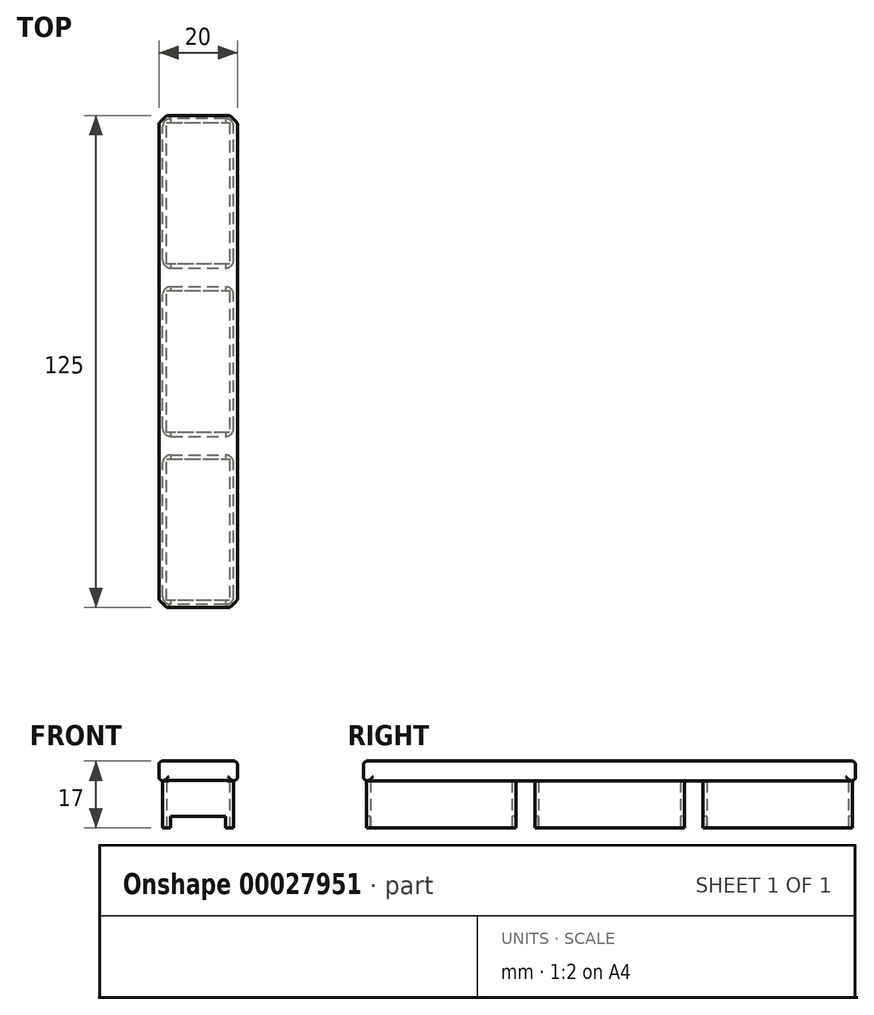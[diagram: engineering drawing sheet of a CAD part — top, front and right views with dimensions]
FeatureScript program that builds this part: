
annotation { "Feature Type Name" : "Feature", "Feature Type Description" : "" }
export const myFeature = defineFeature(function(context is Context, id is Id, definition is map)
    precondition{}
    {
        {
            var Q0;
            Q0=qCreatedBy(makeId("Top.planeOp"),FACE);
            var sketch = newSketch(context, id + "F0", { "sketchPlane" : qUnion([Q0])});
            skLineSegment(sketch, "E0.bottom", {"start": v(-10, 62.5) * mm, "end": v(10, 62.5) * mm});
            skLineSegment(sketch, "E0.top", {"start": v(-10, -62.5) * mm, "end": v(10, -62.5) * mm});
            skLineSegment(sketch, "E0.left", {"start": v(-10, 62.5) * mm, "end": v(-10, -62.5) * mm});
            skLineSegment(sketch, "E0.right", {"start": v(10, 62.5) * mm, "end": v(10, -62.5) * mm});
            skPoint(sketch, "E0.middle", {"position": v(0, 0) * mm});
            skSolve(sketch);
        }
        {
            var Q0;
            Q0=makeQuery(id+"F0.imprint","IMPRINT",FACE,{"disambiguationData":[TD([[makeQuery(id+"F0.imprint","IMPRINT",EDGE,{"derivedFrom":sQuery(id+"F0.wireOp",EDGE,"E0.bottom")}),-1.0]])]});
            extrude(context, id + "F1", {"entities" : qUnion([Q0]), "depth" : 5 * mm});
        }
        {
            var Q0;
            Q0=makeQuery(id+"F1.opExtrude","CAP_FACE",FACE,{"disambiguationData":[OSD([sQuery(id+"F0.wireOp",EDGE,"E0.bottom"),sQuery(id+"F0.wireOp",EDGE,"E0.top"),sQuery(id+"F0.wireOp",EDGE,"E0.left"),sQuery(id+"F0.wireOp",EDGE,"E0.right")])],"isStart":true});
            var sketch = newSketch(context, id + "F2", { "sketchPlane" : qUnion([Q0])});
            skLineSegment(sketch, "E1", {"start": v(0, -62.25) * mm, "end": v(0, 62.25) * mm, "construction": true});
            skPoint(sketch, "E2", {"position": v(-10, 0) * mm});
            skLineSegment(sketch, "E3", {"start": v(-10, 0) * mm, "end": v(10, 0) * mm, "construction": true});
            skPoint(sketch, "E4", {"position": v(0, 0) * mm});
            skLineSegment(sketch, "E5.bottom", {"start": v(-9, 19) * mm, "end": v(9, 19) * mm});
            skLineSegment(sketch, "E5.top", {"start": v(-9, -19) * mm, "end": v(9, -19) * mm});
            skLineSegment(sketch, "E5.left", {"start": v(-9, 19) * mm, "end": v(-9, -19) * mm});
            skLineSegment(sketch, "E5.right", {"start": v(9, 19) * mm, "end": v(9, -19) * mm});
            skLineSegment(sketch, "E6.bottom", {"start": v(-9, 61.75) * mm, "end": v(9, 61.75) * mm});
            skLineSegment(sketch, "E6.top", {"start": v(-9, 23.75) * mm, "end": v(9, 23.75) * mm});
            skLineSegment(sketch, "E6.left", {"start": v(-9, 61.75) * mm, "end": v(-9, 23.75) * mm});
            skLineSegment(sketch, "E6.right", {"start": v(9, 61.75) * mm, "end": v(9, 23.75) * mm});
            skPoint(sketch, "E6.middle", {"position": v(0, 42.75) * mm});
            skLineSegment(sketch, "E7.bottom", {"start": v(-9, -23.75) * mm, "end": v(9, -23.75) * mm});
            skLineSegment(sketch, "E7.top", {"start": v(-9, -61.75) * mm, "end": v(9, -61.75) * mm});
            skLineSegment(sketch, "E7.left", {"start": v(-9, -23.75) * mm, "end": v(-9, -61.75) * mm});
            skLineSegment(sketch, "E7.right", {"start": v(9, -23.75) * mm, "end": v(9, -61.75) * mm});
            skPoint(sketch, "E7.middle", {"position": v(0, -42.75) * mm});
            skSolve(sketch);
        }
        {
            var Q0;
            Q0=makeQuery(id+"F2.imprint","IMPRINT",FACE,{"disambiguationData":[TD([[makeQuery(id+"F2.imprint","IMPRINT",EDGE,{"derivedFrom":sQuery(id+"F2.wireOp",EDGE,"E6.bottom")}),-1.0]])]});
            var Q1;
            Q1=makeQuery(id+"F2.imprint","IMPRINT",FACE,{"disambiguationData":[TD([[makeQuery(id+"F2.imprint","IMPRINT",EDGE,{"derivedFrom":sQuery(id+"F2.wireOp",EDGE,"E5.bottom")}),-1.0]])]});
            var Q2;
            Q2=makeQuery(id+"F2.imprint","IMPRINT",FACE,{"disambiguationData":[TD([[makeQuery(id+"F2.imprint","IMPRINT",EDGE,{"derivedFrom":sQuery(id+"F2.wireOp",EDGE,"E7.bottom")}),-1.0]])]});
            extrude(context, id + "F3", {"entities" : qUnion([Q0, Q1, Q2]), "operationType" : NewBodyOperationType.ADD, "depth" : 12 * mm});
        }
        {
            var Q0;
            Q0=makeQuery(id+"F3.opExtrude","CAP_FACE",FACE,{"disambiguationData":[OSD([sQuery(id+"F2.wireOp",EDGE,"E5.bottom"),sQuery(id+"F2.wireOp",EDGE,"E5.top"),sQuery(id+"F2.wireOp",EDGE,"E5.left"),sQuery(id+"F2.wireOp",EDGE,"E5.right")])],"isStart":false});
            var sketch = newSketch(context, id + "F4", { "sketchPlane" : qUnion([Q0])});
            skLineSegment(sketch, "E8.0", {"start": v(8, 60.75) * mm, "end": v(-8, 60.75) * mm});
            skLineSegment(sketch, "E8.1", {"start": v(8, 24.75) * mm, "end": v(8, 60.75) * mm});
            skLineSegment(sketch, "E8.2", {"start": v(-8, 24.75) * mm, "end": v(8, 24.75) * mm});
            skLineSegment(sketch, "E8.3", {"start": v(-8, 60.75) * mm, "end": v(-8, 24.75) * mm});
            skLineSegment(sketch, "E9.0", {"start": v(8, 18) * mm, "end": v(-8, 18) * mm});
            skLineSegment(sketch, "E9.1", {"start": v(8, -18) * mm, "end": v(8, 18) * mm});
            skLineSegment(sketch, "E9.2", {"start": v(-8, -18) * mm, "end": v(8, -18) * mm});
            skLineSegment(sketch, "E9.3", {"start": v(-8, 18) * mm, "end": v(-8, -18) * mm});
            skLineSegment(sketch, "E10.0", {"start": v(8, -24.75) * mm, "end": v(-8, -24.75) * mm});
            skLineSegment(sketch, "E10.1", {"start": v(8, -60.75) * mm, "end": v(8, -24.75) * mm});
            skLineSegment(sketch, "E10.2", {"start": v(-8, -60.75) * mm, "end": v(8, -60.75) * mm});
            skLineSegment(sketch, "E10.3", {"start": v(-8, -24.75) * mm, "end": v(-8, -60.75) * mm});
            skLineSegment(sketch, "E11.0.0", {"start": v(9, 61.75) * mm, "end": v(-9, 61.75) * mm});
            skLineSegment(sketch, "E11.0.1", {"start": v(-9, 61.75) * mm, "end": v(-9, 23.75) * mm});
            skLineSegment(sketch, "E11.0.2", {"start": v(-9, 23.75) * mm, "end": v(9, 23.75) * mm});
            skLineSegment(sketch, "E11.0.3", {"start": v(9, 23.75) * mm, "end": v(9, 61.75) * mm});
            skLineSegment(sketch, "E12.0.0", {"start": v(9, 19) * mm, "end": v(-9, 19) * mm});
            skLineSegment(sketch, "E12.0.1", {"start": v(-9, 19) * mm, "end": v(-9, -19) * mm});
            skLineSegment(sketch, "E12.0.2", {"start": v(-9, -19) * mm, "end": v(9, -19) * mm});
            skLineSegment(sketch, "E12.0.3", {"start": v(9, -19) * mm, "end": v(9, 19) * mm});
            skLineSegment(sketch, "E13.0.0", {"start": v(9, -23.75) * mm, "end": v(-9, -23.75) * mm});
            skLineSegment(sketch, "E13.0.1", {"start": v(-9, -23.75) * mm, "end": v(-9, -61.75) * mm});
            skLineSegment(sketch, "E13.0.2", {"start": v(-9, -61.75) * mm, "end": v(9, -61.75) * mm});
            skLineSegment(sketch, "E13.0.3", {"start": v(9, -61.75) * mm, "end": v(9, -23.75) * mm});
            skSolve(sketch);
        }
        {
            var Q0;
            Q0=makeQuery(id+"F4.imprint","IMPRINT",FACE,{"disambiguationData":[TD([[makeQuery(id+"F4.imprint","IMPRINT",EDGE,{"derivedFrom":sQuery(id+"F4.wireOp",EDGE,"E8.0")}),1.0]])]});
            var Q1;
            Q1=makeQuery(id+"F4.imprint","IMPRINT",FACE,{"disambiguationData":[TD([[makeQuery(id+"F4.imprint","IMPRINT",EDGE,{"derivedFrom":sQuery(id+"F4.wireOp",EDGE,"E9.0")}),1.0]])]});
            var Q2;
            Q2=makeQuery(id+"F4.imprint","IMPRINT",FACE,{"disambiguationData":[TD([[makeQuery(id+"F4.imprint","IMPRINT",EDGE,{"derivedFrom":sQuery(id+"F4.wireOp",EDGE,"E10.0")}),1.0]])]});
            extrude(context, id + "F5", {"entities" : qUnion([Q0, Q1, Q2]), "operationType" : NewBodyOperationType.REMOVE, "oppositeDirection" : true, "depth" : 12 * mm});
        }
        {
            var Q0;
            Q0=makeQuery(id+"F3.opExtrude","SWEPT_EDGE",EDGE,{"disambiguationData":[OSD([sQuery(id+"F2.wireOp",EDGE,"E6.bottom"),sQuery(id+"F2.wireOp",EDGE,"E6.left")])]});
            var Q1;
            Q1=makeQuery(id+"F3.opExtrude","SWEPT_EDGE",EDGE,{"disambiguationData":[OSD([sQuery(id+"F2.wireOp",EDGE,"E5.bottom"),sQuery(id+"F2.wireOp",EDGE,"E5.left")])]});
            var Q2;
            Q2=makeQuery(id+"F3.opExtrude","SWEPT_EDGE",EDGE,{"disambiguationData":[OSD([sQuery(id+"F2.wireOp",EDGE,"E7.bottom"),sQuery(id+"F2.wireOp",EDGE,"E7.left")])]});
            var Q3;
            Q3=makeQuery(id+"F3.opExtrude","SWEPT_EDGE",EDGE,{"disambiguationData":[OSD([sQuery(id+"F2.wireOp",EDGE,"E6.bottom"),sQuery(id+"F2.wireOp",EDGE,"E6.right")])]});
            var Q4;
            Q4=makeQuery(id+"F3.opExtrude","SWEPT_EDGE",EDGE,{"disambiguationData":[OSD([sQuery(id+"F2.wireOp",EDGE,"E6.top"),sQuery(id+"F2.wireOp",EDGE,"E6.right")])]});
            var Q5;
            Q5=makeQuery(id+"F3.opExtrude","SWEPT_EDGE",EDGE,{"disambiguationData":[OSD([sQuery(id+"F2.wireOp",EDGE,"E5.bottom"),sQuery(id+"F2.wireOp",EDGE,"E5.right")])]});
            var Q6;
            Q6=makeQuery(id+"F3.opExtrude","SWEPT_EDGE",EDGE,{"disambiguationData":[OSD([sQuery(id+"F2.wireOp",EDGE,"E5.top"),sQuery(id+"F2.wireOp",EDGE,"E5.right")])]});
            var Q7;
            Q7=makeQuery(id+"F3.opExtrude","SWEPT_EDGE",EDGE,{"disambiguationData":[OSD([sQuery(id+"F2.wireOp",EDGE,"E5.top"),sQuery(id+"F2.wireOp",EDGE,"E5.left")])]});
            var Q8;
            Q8=makeQuery(id+"F3.opExtrude","SWEPT_EDGE",EDGE,{"disambiguationData":[OSD([sQuery(id+"F2.wireOp",EDGE,"E7.top"),sQuery(id+"F2.wireOp",EDGE,"E7.left")])]});
            var Q9;
            Q9=makeQuery(id+"F3.opExtrude","SWEPT_EDGE",EDGE,{"disambiguationData":[OSD([sQuery(id+"F2.wireOp",EDGE,"E7.top"),sQuery(id+"F2.wireOp",EDGE,"E7.right")])]});
            var Q10;
            Q10=makeQuery(id+"F3.opExtrude","SWEPT_EDGE",EDGE,{"disambiguationData":[OSD([sQuery(id+"F2.wireOp",EDGE,"E7.bottom"),sQuery(id+"F2.wireOp",EDGE,"E7.right")])]});
            var Q11;
            Q11=makeQuery(id+"F3.opExtrude","SWEPT_EDGE",EDGE,{"disambiguationData":[OSD([sQuery(id+"F2.wireOp",EDGE,"E6.top"),sQuery(id+"F2.wireOp",EDGE,"E6.left")])]});
            fillet(context, id + "F6", {"entities" : qUnion([Q0, Q1, Q2, Q3, Q4, Q5, Q6, Q7, Q8, Q9, Q10, Q11]), "radius" : 2 * mm, "tangentPropagation" : true, "allowEdgeOverflow" : false});
        }
        {
            var Q0;
            Q0=makeQuery(id+"F3.opExtrude","SWEPT_FACE",FACE,{"disambiguationData":[OSD([sQuery(id+"F2.wireOp",EDGE,"E6.bottom")])]});
            var sketch = newSketch(context, id + "F7", { "sketchPlane" : qUnion([Q0])});
            skLineSegment(sketch, "E14.bottom", {"start": v(7, -12) * mm, "end": v(-7, -12) * mm});
            skLineSegment(sketch, "E14.top", {"start": v(7, -9) * mm, "end": v(-7, -9) * mm});
            skLineSegment(sketch, "E14.left", {"start": v(7, -12) * mm, "end": v(7, -9) * mm});
            skLineSegment(sketch, "E14.right", {"start": v(-7, -12) * mm, "end": v(-7, -9) * mm});
            skSolve(sketch);
        }
        {
            var Q0;
            Q0=makeQuery(id+"F7.imprint","IMPRINT",FACE,{"disambiguationData":[TD([[makeQuery(id+"F7.imprint","IMPRINT",EDGE,{"derivedFrom":sQuery(id+"F7.wireOp",EDGE,"E14.bottom")}),1.0]])]});
            extrude(context, id + "F8", {"entities" : qUnion([Q0]), "operationType" : NewBodyOperationType.REMOVE, "endBound" : BoundingType.THROUGH_ALL, "oppositeDirection" : true, "depth" : 25 * mm});
        }
        {
            var Q0;
            Q0=makeQuery(id+"F1.opExtrude","SWEPT_EDGE",EDGE,{"disambiguationData":[OSD([sQuery(id+"F0.wireOp",EDGE,"E0.top"),sQuery(id+"F0.wireOp",EDGE,"E0.right")])]});
            var Q1;
            Q1=makeQuery(id+"F1.opExtrude","SWEPT_EDGE",EDGE,{"disambiguationData":[OSD([sQuery(id+"F0.wireOp",EDGE,"E0.top"),sQuery(id+"F0.wireOp",EDGE,"E0.left")])]});
            var Q2;
            Q2=makeQuery(id+"F1.opExtrude","SWEPT_EDGE",EDGE,{"disambiguationData":[OSD([sQuery(id+"F0.wireOp",EDGE,"E0.bottom"),sQuery(id+"F0.wireOp",EDGE,"E0.right")])]});
            var Q3;
            Q3=makeQuery(id+"F1.opExtrude","SWEPT_EDGE",EDGE,{"disambiguationData":[OSD([sQuery(id+"F0.wireOp",EDGE,"E0.bottom"),sQuery(id+"F0.wireOp",EDGE,"E0.left")])]});
            chamfer(context, id + "F9", {"entities" : qUnion([Q0, Q1, Q2, Q3]), "width" : 2 * mm, "tangentPropagation" : true});
        }
        {
            var Q0;
            Q0=makeQuery(id+"F1.opExtrude","CAP_FACE",FACE,{"disambiguationData":[OSD([sQuery(id+"F0.wireOp",EDGE,"E0.bottom"),sQuery(id+"F0.wireOp",EDGE,"E0.top"),sQuery(id+"F0.wireOp",EDGE,"E0.left"),sQuery(id+"F0.wireOp",EDGE,"E0.right")])],"isStart":false});
            var Q1;
            Q1=makeQuery(id+"F1.opExtrude","SWEPT_FACE",FACE,{"disambiguationData":[OSD([sQuery(id+"F0.wireOp",EDGE,"E0.right")])]});
            var Q2;
            Q2=makeQuery(id+"F1.opExtrude","SWEPT_FACE",FACE,{"disambiguationData":[OSD([sQuery(id+"F0.wireOp",EDGE,"E0.top")])]});
            var Q3;
            Q3=makeQuery(id+"F1.opExtrude","SWEPT_FACE",FACE,{"disambiguationData":[OSD([sQuery(id+"F0.wireOp",EDGE,"E0.left")])]});
            var Q4;
            Q4=makeQuery(id+"F1.opExtrude","SWEPT_FACE",FACE,{"disambiguationData":[OSD([sQuery(id+"F0.wireOp",EDGE,"E0.bottom")])]});
            fillet(context, id + "F10", {"entities" : qUnion([Q0, Q1, Q2, Q3, Q4]), "radius" : 1 * mm, "tangentPropagation" : true, "allowEdgeOverflow" : false});
        }
    });
